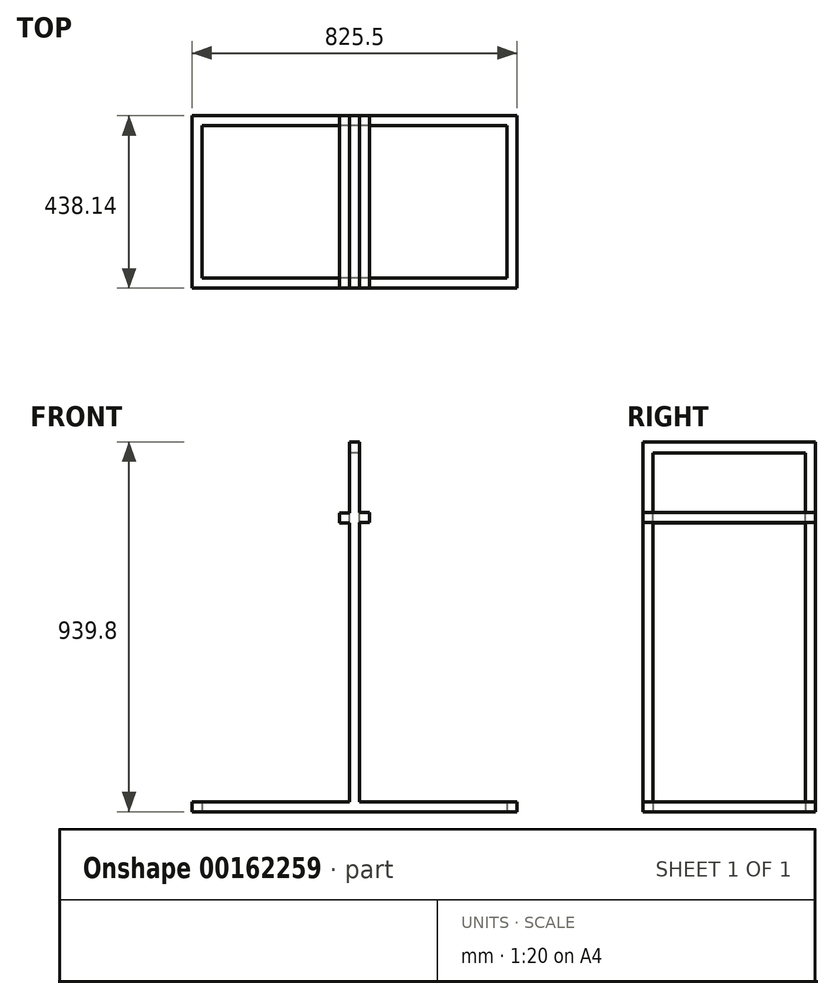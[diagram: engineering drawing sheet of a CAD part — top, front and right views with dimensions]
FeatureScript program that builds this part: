
annotation { "Feature Type Name" : "Feature", "Feature Type Description" : "" }
export const myFeature = defineFeature(function(context is Context, id is Id, definition is map)
    precondition{}
    {
        {
            var Q0;
            Q0=qCreatedBy(makeId("Top.planeOp"),FACE);
            var sketch = newSketch(context, id + "F0", { "sketchPlane" : qUnion([Q0])});
            skLineSegment(sketch, "E0.bottom", {"start": v(412.75, 219.08) * mm, "end": v(-412.75, 219.07) * mm});
            skLineSegment(sketch, "E0.top", {"start": v(412.75, -219.08) * mm, "end": v(-412.75, -219.08) * mm});
            skLineSegment(sketch, "E0.left", {"start": v(412.75, 219.08) * mm, "end": v(412.75, -219.07) * mm});
            skLineSegment(sketch, "E0.right", {"start": v(-412.75, 219.07) * mm, "end": v(-412.75, -219.08) * mm});
            skPoint(sketch, "E0.middle", {"position": v(0, 0) * mm});
            skLineSegment(sketch, "E1.0", {"start": v(12.7, -219.08) * mm, "end": v(12.7, 219.07) * mm});
            skLineSegment(sketch, "E2.0", {"start": v(38.1, -219.08) * mm, "end": v(38.1, 219.07) * mm});
            skLineSegment(sketch, "E3.0", {"start": v(-12.7, -219.08) * mm, "end": v(-12.7, 219.07) * mm});
            skLineSegment(sketch, "E4.0", {"start": v(-38.1, -219.08) * mm, "end": v(-38.1, 219.07) * mm});
            skPoint(sketch, "E5.end.orphan", {"position": v(0, 219.07) * mm});
            skLineSegment(sketch, "E6.bottom", {"start": v(387.35, -193.67) * mm, "end": v(-387.35, -193.68) * mm});
            skLineSegment(sketch, "E6.top", {"start": v(387.35, 193.68) * mm, "end": v(-387.35, 193.67) * mm});
            skLineSegment(sketch, "E6.left", {"start": v(387.35, -193.67) * mm, "end": v(387.35, 193.68) * mm});
            skLineSegment(sketch, "E6.right", {"start": v(-387.35, -193.68) * mm, "end": v(-387.35, 193.67) * mm});
            skSolve(sketch);
        }
        {
            var Q0;
            Q0=qSketchRegion(id+"F0",true);
            extrude(context, id + "F1", {"entities" : qUnion([Q0]), "depth" : 25.4 * mm});
        }
        {
            var Q0;
            {var subQ0=sQuery(id+"F0.wireOp",EDGE,"E6.bottom");var subQ1=sQuery(id+"F0.wireOp",EDGE,"E1.0");var subQ2=makeQuery(id+"F0.imprint","INTERSECT",VERTEX,{"derivedFrom":[subQ1,subQ0]});Q0=makeQuery(id+"F0.imprint","IMPRINT",FACE,{"disambiguationData":[TD([[makeQuery(id+"F0.imprint","IMPRINT",EDGE,{"disambiguationData":[TD([[subQ2,-1.0]])],"derivedFrom":subQ1}),1.0]])]});}
            var Q1;
            {var subQ0=sQuery(id+"F0.wireOp",EDGE,"E1.0");var subQ1=sQuery(id+"F0.wireOp",EDGE,"E0.bottom");var subQ2=makeQuery(id+"F0.imprint","INTERSECT",VERTEX,{"derivedFrom":[subQ1,subQ0]});Q1=makeQuery(id+"F0.imprint","IMPRINT",FACE,{"disambiguationData":[TD([[makeQuery(id+"F0.imprint","IMPRINT",EDGE,{"disambiguationData":[TD([[subQ2,-1.0]])],"derivedFrom":subQ1}),1.0]])]});}
            var Q2;
            {var subQ0=sQuery(id+"F0.wireOp",EDGE,"E1.0");var subQ1=sQuery(id+"F0.wireOp",EDGE,"E0.top");var subQ2=makeQuery(id+"F0.imprint","INTERSECT",VERTEX,{"derivedFrom":[subQ1,subQ0]});Q2=makeQuery(id+"F0.imprint","IMPRINT",FACE,{"disambiguationData":[TD([[makeQuery(id+"F0.imprint","IMPRINT",EDGE,{"disambiguationData":[TD([[subQ2,-1.0]])],"derivedFrom":subQ1}),-1.0]])]});}
            extrude(context, id + "F2", {"entities" : qUnion([Q0, Q1, Q2]), "operationType" : NewBodyOperationType.ADD, "depth" : 939.8 * mm});
        }
        {
            var Q0;
            Q0=makeQuery(id+"F2.opExtrude","SWEPT_FACE",FACE,{"disambiguationData":[OSD([sQuery(id+"F0.wireOp",EDGE,"E3.0")])]});
            var sketch = newSketch(context, id + "F3", { "sketchPlane" : qUnion([Q0])});
            skLineSegment(sketch, "E7.bottom", {"start": v(193.67, -2.54) * mm, "end": v(-193.68, -2.54) * mm});
            skLineSegment(sketch, "E7.top", {"start": v(193.67, 911.86) * mm, "end": v(-193.68, 911.86) * mm});
            skLineSegment(sketch, "E7.left", {"start": v(193.67, -2.54) * mm, "end": v(193.67, 737.56) * mm});
            skLineSegment(sketch, "E7.right", {"start": v(-193.68, -2.54) * mm, "end": v(-193.68, 737.56) * mm});
            skPoint(sketch, "E7.middle", {"position": v(0, 454.66) * mm});
            skLineSegment(sketch, "E8.trimOffspring", {"start": v(-193.68, 737.56) * mm, "end": v(-193.68, 911.86) * mm});
            skLineSegment(sketch, "E9.trimOffspring", {"start": v(193.67, 737.56) * mm, "end": v(193.67, 911.86) * mm});
            skSolve(sketch);
        }
        {
            var Q0;
            Q0=qSketchRegion(id+"F3",true);
            extrude(context, id + "F4", {"entities" : qUnion([Q0]), "operationType" : NewBodyOperationType.REMOVE, "oppositeDirection" : true, "depth" : 25.4 * mm});
        }
        {
            var Q0;
            {var subQ0=sQuery(id+"F0.wireOp",EDGE,"E6.bottom");var subQ1=sQuery(id+"F0.wireOp",EDGE,"E0.right");var subQ2=sQuery(id+"F0.wireOp",EDGE,"E0.top");var subQ3=sQuery(id+"F0.wireOp",EDGE,"E0.bottom");var subQ4=sQuery(id+"F0.wireOp",EDGE,"E6.top");var subQ5=sQuery(id+"F0.wireOp",EDGE,"E6.right");Q0=makeQuery(id+"F2.boolean.opBoolean","SPLIT",FACE,{"disambiguationData":[TD([makeQuery(id+"F1.opExtrude","SWEPT_FACE",FACE,{"disambiguationData":[OSD([subQ1])]})])],"derivedFrom":makeQuery(id+"F1.opExtrude","CAP_FACE",FACE,{"disambiguationData":[OSD([subQ3,subQ2,sQuery(id+"F0.wireOp",EDGE,"E0.left"),subQ1,subQ0,subQ4,sQuery(id+"F0.wireOp",EDGE,"E6.left"),subQ5])],"isStart":false})});}
            var sketch = newSketch(context, id + "F5", { "sketchPlane" : qUnion([Q0])});
            skCircle(sketch, "E10", {"center": v(-399.58, 117.47) * mm, "radius": 25.4 * mm});
            skCircle(sketch, "E11", {"center": v(-399.99, 41.27) * mm, "radius": 25.4 * mm});
            skCircle(sketch, "E12", {"center": v(-401.61, -34.93) * mm, "radius": 25.4 * mm});
            skCircle(sketch, "E13", {"center": v(-400.8, -117.48) * mm, "radius": 25.4 * mm});
            skLineSegment(sketch, "E14", {"start": v(0, 0) * mm, "end": v(0, 244.32) * mm, "construction": true});
            skCircle(sketch, "E15.MirrorC", {"center": v(399.58, 117.47) * mm, "radius": 25.4 * mm});
            skCircle(sketch, "E16.MirrorC", {"center": v(399.99, 41.27) * mm, "radius": 25.4 * mm});
            skCircle(sketch, "E17.MirrorC", {"center": v(401.61, -34.93) * mm, "radius": 25.4 * mm});
            skCircle(sketch, "E18.MirrorC", {"center": v(400.8, -117.48) * mm, "radius": 25.4 * mm});
            skSolve(sketch);
        }
        {
            var Q0;
            Q0=sQuery(id+"F5.wireOp",EDGE,"E10");
            var Q1;
            Q1=sQuery(id+"F5.wireOp",EDGE,"E11");
            var Q2;
            Q2=sQuery(id+"F5.wireOp",EDGE,"E12");
            var Q3;
            Q3=sQuery(id+"F5.wireOp",EDGE,"E13");
            var Q4;
            Q4=sQuery(id+"F5.wireOp",EDGE,"E18.MirrorC");
            var Q5;
            Q5=sQuery(id+"F5.wireOp",EDGE,"E17.MirrorC");
            var Q6;
            Q6=sQuery(id+"F5.wireOp",EDGE,"E16.MirrorC");
            var Q7;
            Q7=sQuery(id+"F5.wireOp",EDGE,"E15.MirrorC");
            extrude(context, id + "F6", {"bodyType" : ToolBodyType.SURFACE, "operationType" : NewBodyOperationType.ADD, "surfaceEntities" : qUnion([Q0, Q1, Q2, Q3, Q4, Q5, Q6, Q7]), "depth" : 228.6 * mm});
        }
        {
            var Q0;
            Q0=makeQuery(id+"F2.opExtrude","SWEPT_FACE",FACE,{"disambiguationData":[OSD([sQuery(id+"F0.wireOp",EDGE,"E3.0")])]});
            var sketch = newSketch(context, id + "F7", { "sketchPlane" : qUnion([Q0])});
            skLineSegment(sketch, "E19", {"start": v(-219.07, 759.46) * mm, "end": v(219.08, 759.46) * mm});
            skLineSegment(sketch, "E20", {"start": v(219.07, 759.46) * mm, "end": v(219.08, 734.06) * mm});
            skLineSegment(sketch, "E21", {"start": v(219.08, 734.06) * mm, "end": v(-219.07, 734.06) * mm});
            skLineSegment(sketch, "E22", {"start": v(-219.07, 734.06) * mm, "end": v(-219.07, 759.46) * mm});
            skSolve(sketch);
        }
        {
            var Q0;
            {var subQ0=sQuery(id+"F7.wireOp",EDGE,"E20");Q0=makeQuery(id+"F7.imprint","IMPRINT",FACE,{"disambiguationData":[TD([[makeQuery(id+"F7.imprint","IMPRINT",EDGE,{"derivedFrom":subQ0}),-1.0]])]});}
            var Q1;
            {var subQ0=sQuery(id+"F7.wireOp",EDGE,"E19");var subQ1=makeQuery(id+"F4.boolean.opBoolean","COPY",EDGE,{"derivedFrom":makeQuery(id+"F4.opExtrude","CAP_EDGE",EDGE,{"disambiguationData":[OSD([sQuery(id+"F3.wireOp",EDGE,"E7.right"),sQuery(id+"F3.wireOp",EDGE,"E8.trimOffspring")])],"isStart":true})});var subQ2=makeQuery(id+"F7.imprint","INTERSECT",VERTEX,{"derivedFrom":[subQ1,subQ0]});Q1=makeQuery(id+"F7.imprint","IMPRINT",FACE,{"disambiguationData":[TD([[makeQuery(id+"F7.imprint","IMPRINT",EDGE,{"disambiguationData":[TD([[subQ2,-1.0]])],"derivedFrom":subQ0}),-1.0]])]});}
            var Q2;
            {var subQ0=sQuery(id+"F7.wireOp",EDGE,"E22");Q2=makeQuery(id+"F7.imprint","IMPRINT",FACE,{"disambiguationData":[TD([[makeQuery(id+"F7.imprint","IMPRINT",EDGE,{"derivedFrom":subQ0}),1.0]])]});}
            extrude(context, id + "F8", {"entities" : qUnion([Q0, Q1, Q2]), "operationType" : NewBodyOperationType.ADD, "depth" : 25.4 * mm});
        }
        {
            var Q0;
            Q0=makeQuery(id+"F2.opExtrude","SWEPT_FACE",FACE,{"disambiguationData":[OSD([sQuery(id+"F0.wireOp",EDGE,"E1.0")])]});
            var sketch = newSketch(context, id + "F9", { "sketchPlane" : qUnion([Q0])});
            skLineSegment(sketch, "E23.bottom", {"start": v(-219.08, 759.62) * mm, "end": v(219.07, 759.62) * mm});
            skLineSegment(sketch, "E23.top", {"start": v(-219.08, 734.22) * mm, "end": v(219.07, 734.22) * mm});
            skLineSegment(sketch, "E23.left", {"start": v(-219.08, 759.62) * mm, "end": v(-219.08, 734.22) * mm});
            skLineSegment(sketch, "E23.right", {"start": v(219.07, 759.62) * mm, "end": v(219.07, 734.22) * mm});
            skSolve(sketch);
        }
        {
            var Q0;
            Q0=qSketchRegion(id+"F9",true);
            extrude(context, id + "F10", {"entities" : qUnion([Q0]), "operationType" : NewBodyOperationType.ADD, "depth" : 25.4 * mm});
        }
    });
